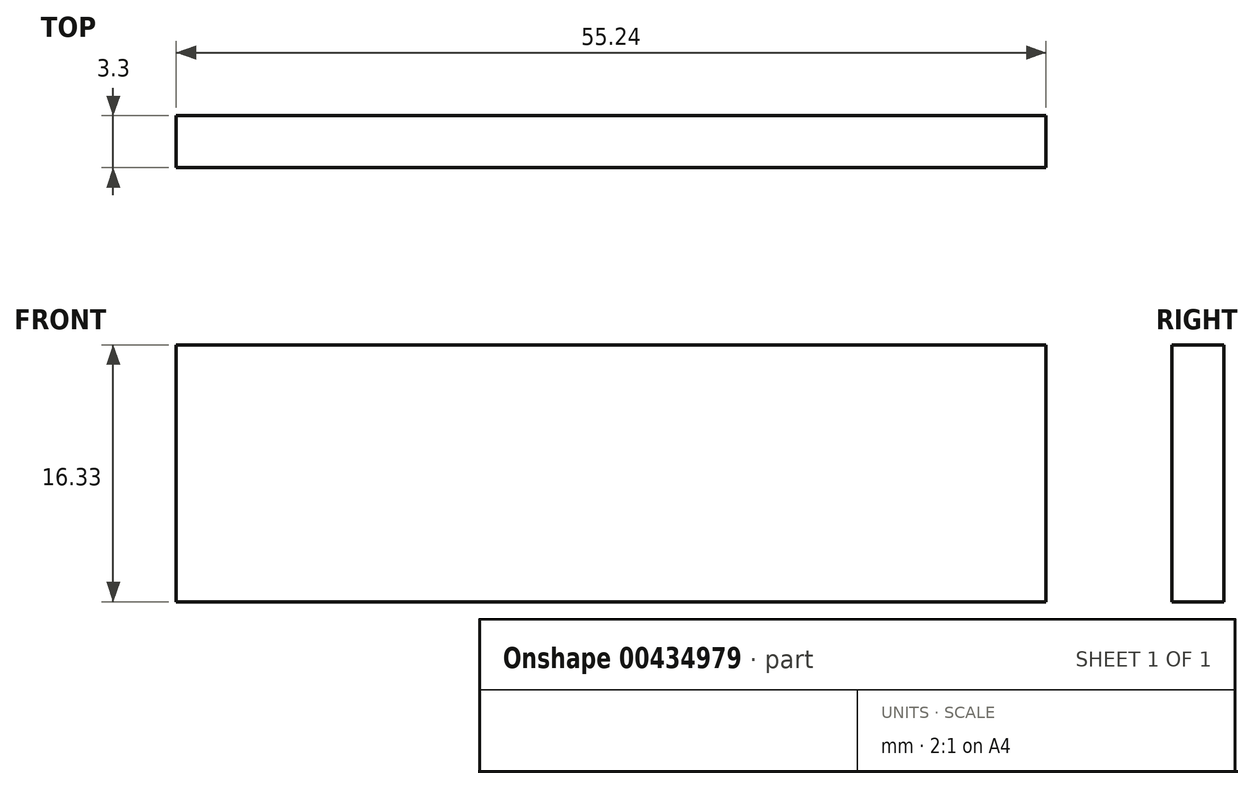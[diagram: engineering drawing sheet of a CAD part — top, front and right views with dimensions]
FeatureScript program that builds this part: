
annotation { "Feature Type Name" : "Feature", "Feature Type Description" : "" }
export const myFeature = defineFeature(function(context is Context, id is Id, definition is map)
    precondition{}
    {
        {
            var Q0;
            Q0=qCreatedBy(makeId("Front.planeOp"),FACE);
            var sketch = newSketch(context, id + "F0", { "sketchPlane" : qUnion([Q0])});
            skLineSegment(sketch, "E0.bottom", {"start": v(0, 0) * mm, "end": v(55.24, 0) * mm});
            skLineSegment(sketch, "E0.top", {"start": v(0, 16.33) * mm, "end": v(55.24, 16.33) * mm});
            skLineSegment(sketch, "E0.left", {"start": v(0, 0) * mm, "end": v(0, 16.33) * mm});
            skLineSegment(sketch, "E0.right", {"start": v(55.24, 0) * mm, "end": v(55.24, 16.33) * mm});
            skSolve(sketch);
        }
        {
            var Q0;
            Q0 = qSketchRegion(id + "F0", true);
            extrude(context, id + "F1", {"entities" : qUnion([Q0]), "depth" : 3.3 * mm});
        }
    });
